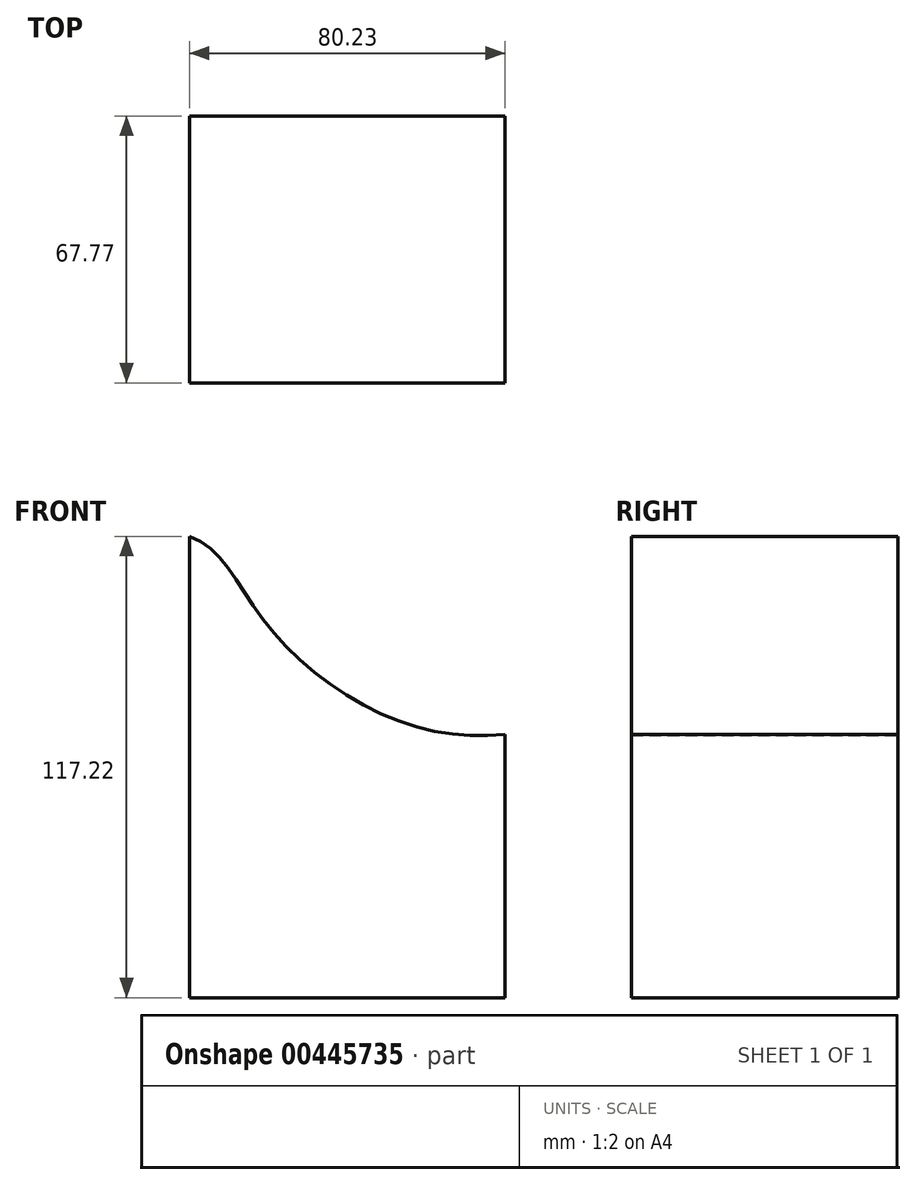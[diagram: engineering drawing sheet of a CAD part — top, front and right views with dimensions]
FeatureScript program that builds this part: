
annotation { "Feature Type Name" : "Feature", "Feature Type Description" : "" }
export const myFeature = defineFeature(function(context is Context, id is Id, definition is map)
    precondition{}
    {
        {
            var Q0;
            Q0=qCreatedBy(makeId("Front.planeOp"),FACE);
            var sketch = newSketch(context, id + "F0", { "sketchPlane" : qUnion([Q0])});
            skFitSpline(sketch, "E0", {"points": [v(-63.92, 43.52) * mm, v(-41.25, 40.34) * mm, v(-24.48, 18.81) * mm, v(13.6, -6.57) * mm, v(53.26, -6.12) * mm], "startDerivative": vector(121.38, 4.15) * mm, "endDerivative": vector(144.25, 22.42) * mm});
            skSolve(sketch);
        }
        {
            var Q0;
            Q0 = qSketchRegion(id + "F0", true);
            var Q1;
            Q1=sQuery(id+"F0.wireOp",EDGE,"E0");
            extrude(context, id + "F1", {"entities" : qUnion([Q0]), "bodyType" : ToolBodyType.SURFACE, "surfaceEntities" : qUnion([Q1]), "depth" : 50.8 * mm, "hasSecondDirection" : true, "secondDirectionOppositeDirection" : true, "secondDirectionDepth" : 50.8 * mm});
        }
        {
            var Q0;
            Q0=qCreatedBy(makeId("Top.planeOp"),FACE);
            cPlane(context, id + "F2", {"entities" : qUnion([Q0]), "cplaneType" : CPlaneType.OFFSET, "offset" : 75.18 * mm, "oppositeDirection" : true, "width" : 152.4 * mm, "height" : 152.4 * mm});
        }
        {
            var Q0;
            Q0=qCreatedBy(id+"F2.planeOp",FACE);
            var sketch = newSketch(context, id + "F3", { "sketchPlane" : qUnion([Q0])});
            skLineSegment(sketch, "E1.bottom", {"start": v(-44.77, 33.64) * mm, "end": v(35.46, 33.64) * mm});
            skLineSegment(sketch, "E1.top", {"start": v(-44.77, -34.13) * mm, "end": v(35.46, -34.13) * mm});
            skLineSegment(sketch, "E1.left", {"start": v(-44.77, 33.64) * mm, "end": v(-44.77, -34.13) * mm});
            skLineSegment(sketch, "E1.right", {"start": v(35.46, 33.64) * mm, "end": v(35.46, -34.13) * mm});
            skSolve(sketch);
        }
        {
            var Q0;
            Q0 = qSketchRegion(id + "F3", true);
            var Q1;
            Q1=makeQuery(id+"F1.opExtrude","SWEPT_FACE",FACE,{"disambiguationData":[OSD([sQuery(id+"F0.wireOp",EDGE,"E0")])]});
            extrude(context, id + "F4", {"entities" : qUnion([Q0]), "endBound" : BoundingType.UP_TO_SURFACE, "endBoundEntityFace" : qUnion([Q1]), "depth" : 25.4 * mm});
        }
    });
